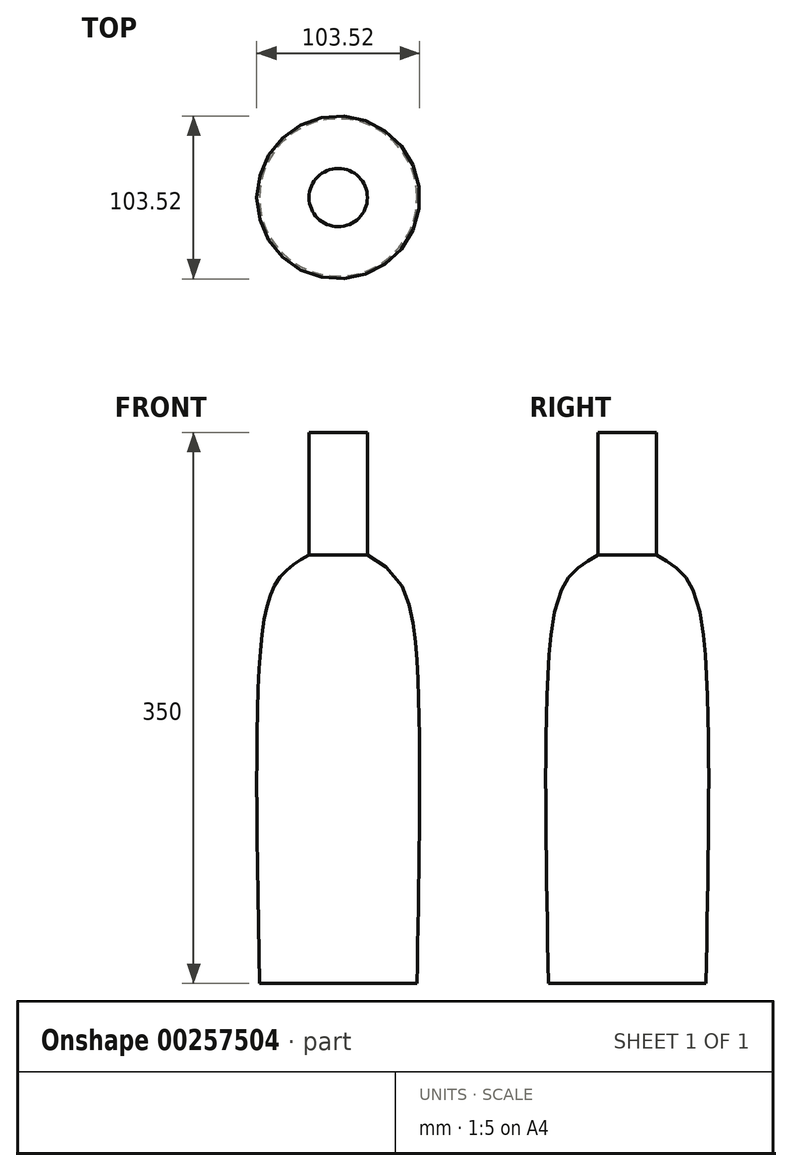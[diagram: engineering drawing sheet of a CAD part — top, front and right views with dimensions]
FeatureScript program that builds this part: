
annotation { "Feature Type Name" : "Feature", "Feature Type Description" : "" }
export const myFeature = defineFeature(function(context is Context, id is Id, definition is map)
    precondition{}
    {
        {
            var Q0;
            Q0=qCreatedBy(makeId("Front.planeOp"),FACE);
            var sketch = newSketch(context, id + "F0", { "sketchPlane" : qUnion([Q0])});
            skLineSegment(sketch, "E0.bottom", {"start": v(0, 0) * mm, "end": v(50, 0) * mm});
            skLineSegment(sketch, "E0.left", {"start": v(0, 0) * mm, "end": v(0, 350) * mm});
            skFitSpline(sketch, "E1", {"points": [v(50, 0) * mm, v(50, 203.6) * mm, v(38.14, 256.56) * mm, v(18.51, 272.12) * mm], "startDerivative": vector(8.53, 434.4) * mm, "endDerivative": vector(-116.05, 66.48) * mm});
            skLineSegment(sketch, "E2", {"start": v(18.51, 272.12) * mm, "end": v(18.51, 350) * mm});
            skLineSegment(sketch, "E3", {"start": v(0, 350) * mm, "end": v(18.51, 350) * mm});
            skSolve(sketch);
        }
        {
            var Q0;
            Q0 = qSketchRegion(id + "F0", true);
            var Q1;
            Q1=sQuery(id+"F0.wireOp",EDGE,"E0.left");
            revolve(context, id + "F1", {"entities" : qUnion([Q0]), "axis" : qUnion([Q1]), "revolveType" : RevolveType.FULL});
        }
    });
